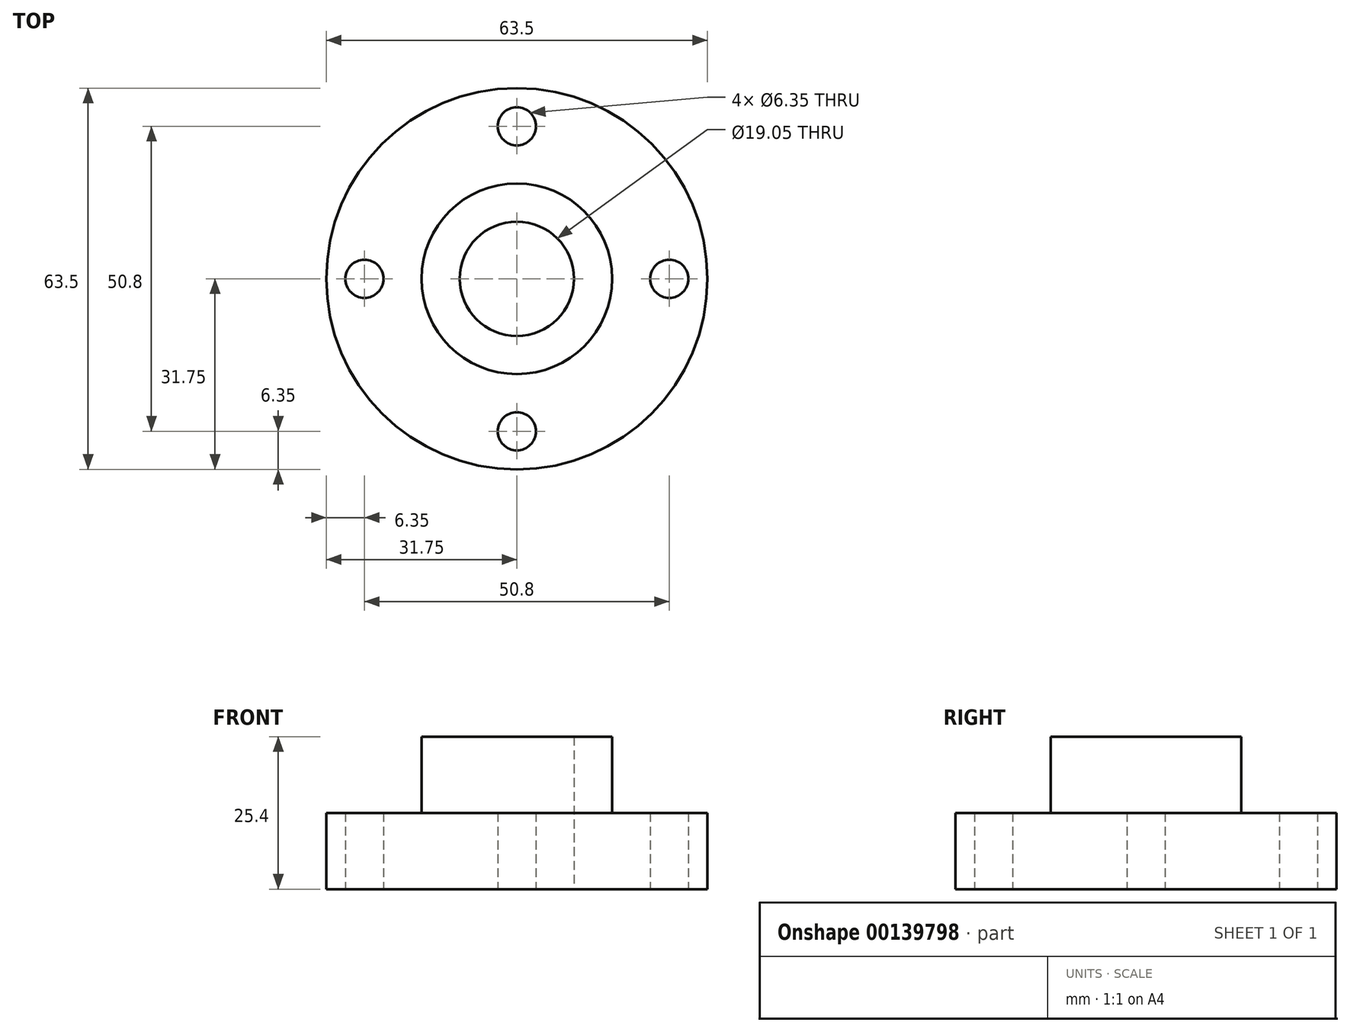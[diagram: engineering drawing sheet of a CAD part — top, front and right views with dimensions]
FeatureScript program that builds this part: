
annotation { "Feature Type Name" : "Feature", "Feature Type Description" : "" }
export const myFeature = defineFeature(function(context is Context, id is Id, definition is map)
    precondition{}
    {
        {
            var Q0;
            Q0=qCreatedBy(makeId("Top.planeOp"),FACE);
            var sketch = newSketch(context, id + "F0", { "sketchPlane" : qUnion([Q0])});
            skCircle(sketch, "E0", {"center": v(0, 0) * mm, "radius": 31.75 * mm});
            skCircle(sketch, "E1", {"center": v(0, 0) * mm, "radius": 15.88 * mm});
            skCircle(sketch, "E2", {"center": v(0, 0) * mm, "radius": 9.53 * mm});
            skCircle(sketch, "E3", {"center": v(0, 0) * mm, "radius": 25.4 * mm, "construction": true});
            skLineSegment(sketch, "E4", {"start": v(0, 49.26) * mm, "end": v(0, -51.56) * mm, "construction": true});
            skLineSegment(sketch, "E5", {"start": v(-62.62, 0) * mm, "end": v(57.73, 0) * mm, "construction": true});
            skCircle(sketch, "E6", {"center": v(0, 25.4) * mm, "radius": 3.18 * mm});
            skCircle(sketch, "E7", {"center": v(25.4, 0) * mm, "radius": 3.18 * mm});
            skCircle(sketch, "E8", {"center": v(-25.4, 0) * mm, "radius": 3.18 * mm});
            skCircle(sketch, "E9", {"center": v(0, -25.4) * mm, "radius": 3.18 * mm});
            skSolve(sketch);
        }
        {
            var Q0;
            Q0=makeQuery(id+"F0.imprint","IMPRINT",FACE,{"disambiguationData":[TD([[makeQuery(id+"F0.imprint","IMPRINT",EDGE,{"derivedFrom":sQuery(id+"F0.wireOp",EDGE,"E1")}),1.0]])]});
            extrude(context, id + "F1", {"entities" : qUnion([Q0]), "depth" : 25.4 * mm});
        }
        {
            var Q0;
            Q0=makeQuery(id+"F0.imprint","IMPRINT",FACE,{"disambiguationData":[TD([[makeQuery(id+"F0.imprint","IMPRINT",EDGE,{"derivedFrom":sQuery(id+"F0.wireOp",EDGE,"E0")}),1.0]])]});
            extrude(context, id + "F2", {"entities" : qUnion([Q0]), "operationType" : NewBodyOperationType.ADD, "depth" : 12.7 * mm});
        }
    });
